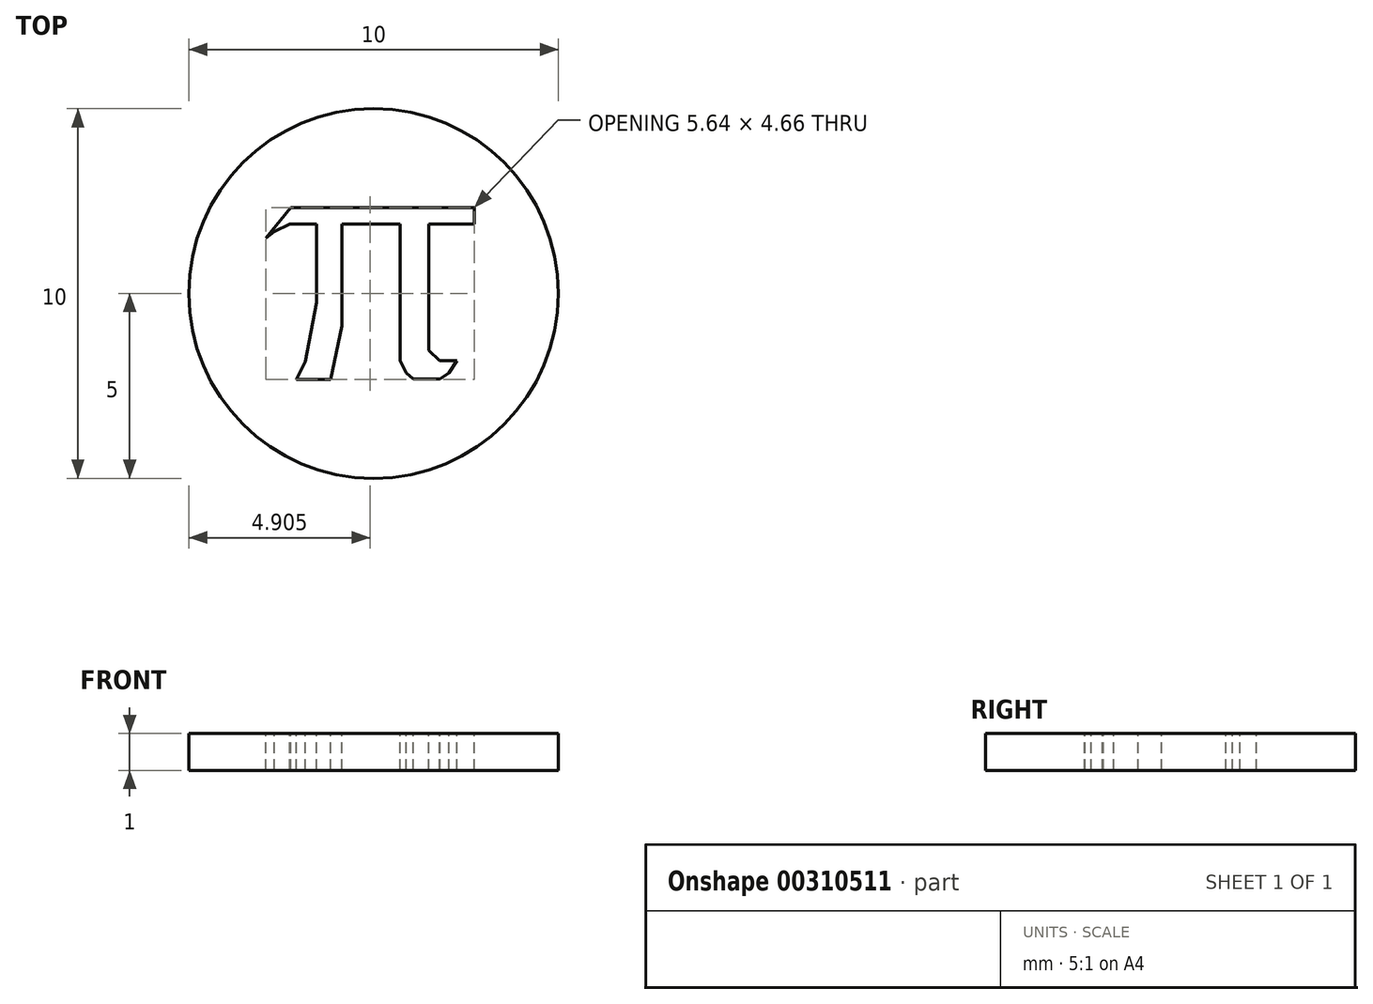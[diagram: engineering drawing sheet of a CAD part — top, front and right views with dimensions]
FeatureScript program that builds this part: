
annotation { "Feature Type Name" : "Feature", "Feature Type Description" : "" }
export const myFeature = defineFeature(function(context is Context, id is Id, definition is map)
    precondition{}
    {
        {
            var Q0;
            Q0=qCreatedBy(makeId("Top.planeOp"),FACE);
            var sketch = newSketch(context, id + "F0", { "sketchPlane" : qUnion([Q0])});
            skCircle(sketch, "E0", {"center": v(0, 0) * mm, "radius": 5 * mm});
            skSolve(sketch);
        }
        {
            var Q0;
            Q0 = qSketchRegion(id + "F0", true);
            extrude(context, id + "F1", {"entities" : qUnion([Q0]), "depth" : 1 * mm});
        }
        {
            var Q0;
            Q0=makeQuery(id+"F1.opExtrude","CAP_FACE",FACE,{"disambiguationData":[OSD([sQuery(id+"F0.wireOp",EDGE,"E0")])],"isStart":false});
            var sketch = newSketch(context, id + "F2", { "sketchPlane" : qUnion([Q0])});
            skLineSegment(sketch, "E1", {"start": v(2.72, 2.33) * mm, "end": v(2.72, 1.88) * mm});
            skLineSegment(sketch, "E2", {"start": v(2.72, 1.88) * mm, "end": v(-2.27, 1.88) * mm});
            skLineSegment(sketch, "E3", {"start": v(-2.27, 1.88) * mm, "end": v(-2.68, 1.68) * mm});
            skLineSegment(sketch, "E4", {"start": v(-2.68, 1.68) * mm, "end": v(-2.91, 1.5) * mm});
            skLineSegment(sketch, "E5", {"start": v(-2.91, 1.5) * mm, "end": v(-2.25, 2.33) * mm});
            skLineSegment(sketch, "E6", {"start": v(-2.25, 2.33) * mm, "end": v(2.72, 2.33) * mm});
            skLineSegment(sketch, "E7", {"start": v(-1.54, 1.88) * mm, "end": v(-1.54, 0.17) * mm});
            skLineSegment(sketch, "E8", {"start": v(-1.54, 0.17) * mm, "end": v(-1.54, -0.25) * mm});
            skLineSegment(sketch, "E9", {"start": v(-1.54, -0.25) * mm, "end": v(-1.85, -1.84) * mm});
            skLineSegment(sketch, "E10", {"start": v(-1.85, -1.84) * mm, "end": v(-2.09, -2.33) * mm});
            skLineSegment(sketch, "E11", {"start": v(-2.09, -2.33) * mm, "end": v(-1.17, -2.33) * mm});
            skLineSegment(sketch, "E12", {"start": v(-1.17, -2.33) * mm, "end": v(-0.85, -0.87) * mm});
            skLineSegment(sketch, "E13", {"start": v(-0.85, -0.87) * mm, "end": v(-0.85, 1.88) * mm});
            skLineSegment(sketch, "E14", {"start": v(0.72, 1.88) * mm, "end": v(0.72, -1.82) * mm});
            skLineSegment(sketch, "E15", {"start": v(0.72, -1.82) * mm, "end": v(0.88, -2.15) * mm});
            skLineSegment(sketch, "E16", {"start": v(0.88, -2.15) * mm, "end": v(1.07, -2.3) * mm});
            skLineSegment(sketch, "E17", {"start": v(0.92, -2.3) * mm, "end": v(1.07, -2.3) * mm});
            skLineSegment(sketch, "E18", {"start": v(0.92, -2.3) * mm, "end": v(1.8, -2.3) * mm});
            skLineSegment(sketch, "E19", {"start": v(1.8, -2.3) * mm, "end": v(2.04, -2.15) * mm});
            skLineSegment(sketch, "E20", {"start": v(2.04, -2.15) * mm, "end": v(2.25, -1.82) * mm});
            skLineSegment(sketch, "E21", {"start": v(2.25, -1.82) * mm, "end": v(1.78, -1.82) * mm});
            skLineSegment(sketch, "E22", {"start": v(1.78, -1.82) * mm, "end": v(1.49, -1.54) * mm});
            skLineSegment(sketch, "E23", {"start": v(1.49, -1.54) * mm, "end": v(1.49, 1.88) * mm});
            skSolve(sketch);
        }
        {
            var Q0;
            Q0 = qSketchRegion(id + "F2", true);
            extrude(context, id + "F3", {"entities" : qUnion([Q0]), "operationType" : NewBodyOperationType.REMOVE, "oppositeDirection" : true, "depth" : 1 * mm});
        }
    });
